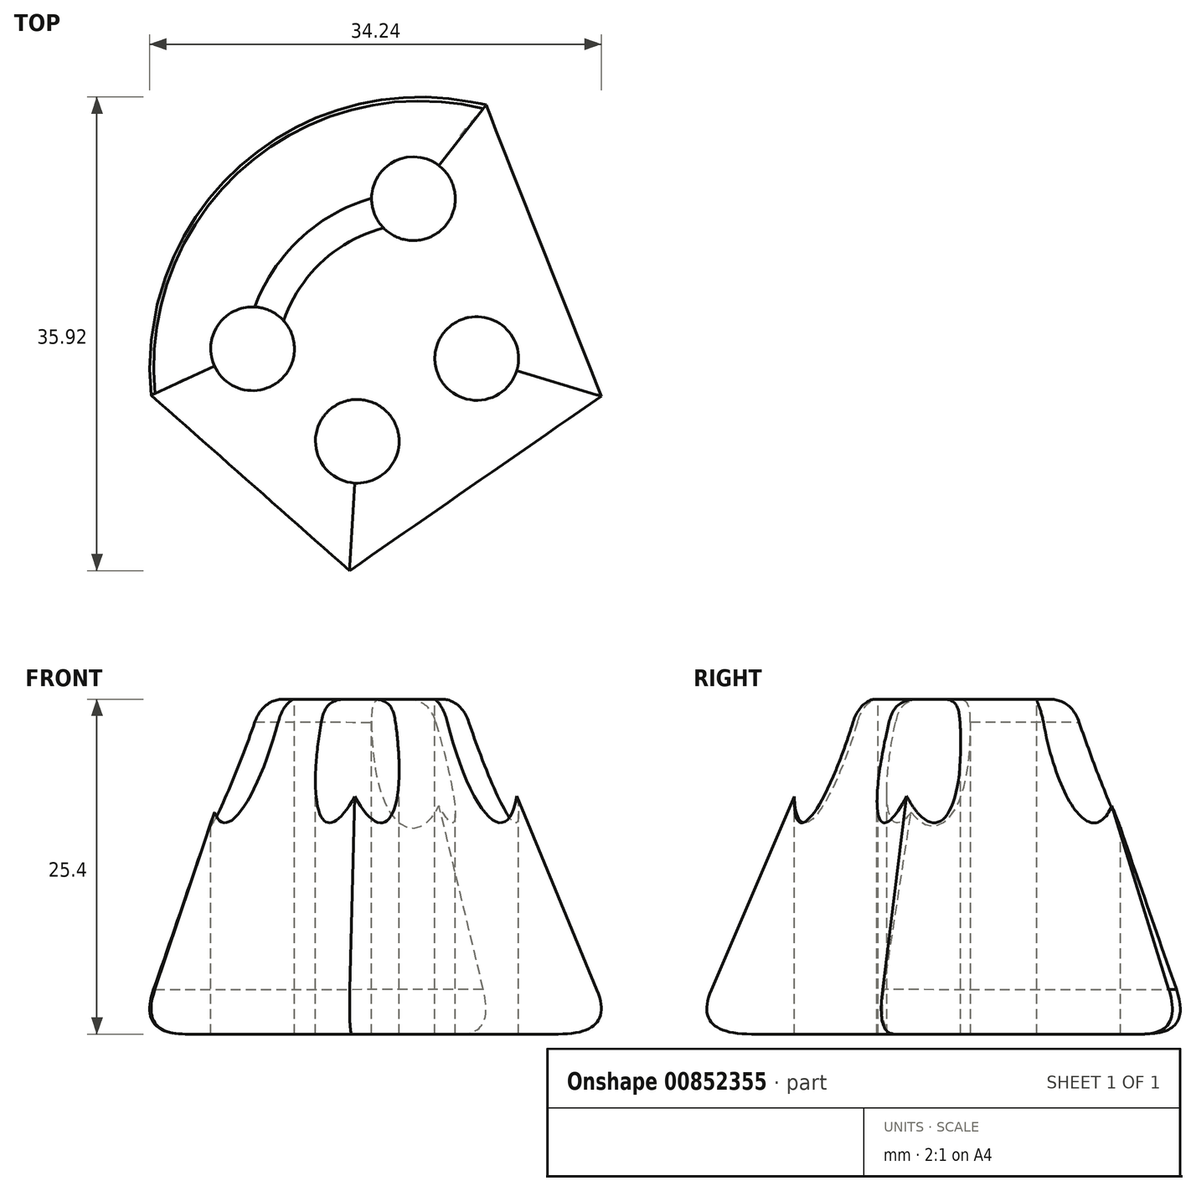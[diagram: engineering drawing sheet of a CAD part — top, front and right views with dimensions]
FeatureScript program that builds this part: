
annotation { "Feature Type Name" : "Feature", "Feature Type Description" : "" }
export const myFeature = defineFeature(function(context is Context, id is Id, definition is map)
    precondition{}
    {
        {
            var Q0;
            Q0=qCreatedBy(makeId("Top.planeOp"),FACE);
            var sketch = newSketch(context, id + "F0", { "sketchPlane" : qUnion([Q0])});
            skArc(sketch, "E0", {"start": v(-21.4, 41.04) * mm, "mid": v(-40.95, 36.53) * mm, "end": v(-48.27, 17.85) * mm});
            skLineSegment(sketch, "E1", {"start": v(-48.27, 17.85) * mm, "end": v(-32.43, 3.85) * mm});
            skLineSegment(sketch, "E2", {"start": v(-32.43, 3.85) * mm, "end": v(-12.23, 17.85) * mm});
            skLineSegment(sketch, "E3", {"start": v(-12.23, 17.85) * mm, "end": v(-21.4, 41.04) * mm});
            skSolve(sketch);
        }
        {
            var Q0;
            Q0=qCreatedBy(makeId("Top.planeOp"),FACE);
            cPlane(context, id + "F1", {"entities" : qUnion([Q0]), "cplaneType" : CPlaneType.OFFSET, "offset" : 25.4 * mm, "width" : 152.4 * mm, "height" : 152.4 * mm});
        }
        {
            var Q0;
            Q0=qCreatedBy(id+"F1.planeOp",FACE);
            var sketch = newSketch(context, id + "F2", { "sketchPlane" : qUnion([Q0])});
            skLineSegment(sketch, "E4.0", {"start": v(-31.79, 14.74) * mm, "end": v(-22.72, 21.03) * mm});
            skLineSegment(sketch, "E4.1", {"start": v(-39.72, 21.76) * mm, "end": v(-31.79, 14.74) * mm});
            skArc(sketch, "E4.2", {"start": v(-27.52, 33.15) * mm, "mid": v(-35.71, 29.7) * mm, "end": v(-39.72, 21.76) * mm});
            skLineSegment(sketch, "E4.3", {"start": v(-22.72, 21.03) * mm, "end": v(-27.52, 33.15) * mm});
            skSolve(sketch);
        }
        {
            var Q0;
            Q0=makeQuery(id+"F0.imprint","IMPRINT",FACE,{"disambiguationData":[TD([[makeQuery(id+"F0.imprint","IMPRINT",EDGE,{"derivedFrom":sQuery(id+"F0.wireOp",EDGE,"E0")}),1.0]])]});
            var Q1;
            Q1=makeQuery(id+"F2.imprint","IMPRINT",FACE,{"disambiguationData":[TD([[makeQuery(id+"F2.imprint","IMPRINT",EDGE,{"derivedFrom":sQuery(id+"F2.wireOp",EDGE,"E4.0")}),1.0]])]});
            loft(context, id + "F3", {"sheetProfilesArray" : [{ "sheetProfileEntities" : qUnion([Q0]) }, { "sheetProfileEntities" : qUnion([Q1]) }]});
        }
        {
            var Q0;
            Q0=makeQuery(id+"F3.opLoft","MID_CAP_EDGE",EDGE,{"disambiguationData":[OSD([sQuery(id+"F2.wireOp",EDGE,"E4.1"),sQuery(id+"F2.wireOp",EDGE,"E4.2"),sQuery(id+"F2.wireOp",EDGE,"E4.3")])],"capPos":1.0});
            var Q1;
            Q1=makeQuery(id+"F3.opLoft","MID_CAP_EDGE",EDGE,{"disambiguationData":[OSD([sQuery(id+"F2.wireOp",EDGE,"E4.0"),sQuery(id+"F2.wireOp",EDGE,"E4.2"),sQuery(id+"F2.wireOp",EDGE,"E4.3")])],"capPos":1.0});
            var Q2;
            Q2=makeQuery(id+"F3.opLoft","MID_CAP_EDGE",EDGE,{"disambiguationData":[OSD([sQuery(id+"F2.wireOp",EDGE,"E4.0"),sQuery(id+"F2.wireOp",EDGE,"E4.1"),sQuery(id+"F2.wireOp",EDGE,"E4.3")])],"capPos":1.0});
            var Q3;
            Q3=makeQuery(id+"F3.opLoft","MID_CAP_EDGE",EDGE,{"disambiguationData":[OSD([sQuery(id+"F2.wireOp",EDGE,"E4.0"),sQuery(id+"F2.wireOp",EDGE,"E4.1"),sQuery(id+"F2.wireOp",EDGE,"E4.2")])],"capPos":1.0});
            fillet(context, id + "F4", {"entities" : qUnion([Q0, Q1, Q2, Q3]), "radius" : 2.54 * mm, "tangentPropagation" : true, "rho" : 0.5, "crossSection" : FilletCrossSection.CONIC, "allowEdgeOverflow" : false});
        }
        {
            var Q0;
            Q0=makeQuery(id+"F3.opLoft","MID_CAP_EDGE",EDGE,{"disambiguationData":[OSD([sQuery(id+"F0.wireOp",EDGE,"E0"),sQuery(id+"F0.wireOp",EDGE,"E1"),sQuery(id+"F0.wireOp",EDGE,"E3")])],"capPos":0.0});
            var Q1;
            Q1=makeQuery(id+"F3.opLoft","MID_CAP_EDGE",EDGE,{"disambiguationData":[OSD([sQuery(id+"F0.wireOp",EDGE,"E0"),sQuery(id+"F0.wireOp",EDGE,"E2"),sQuery(id+"F0.wireOp",EDGE,"E3")])],"capPos":0.0});
            var Q2;
            Q2=makeQuery(id+"F3.opLoft","MID_CAP_EDGE",EDGE,{"disambiguationData":[OSD([sQuery(id+"F0.wireOp",EDGE,"E1"),sQuery(id+"F0.wireOp",EDGE,"E2"),sQuery(id+"F0.wireOp",EDGE,"E3")])],"capPos":0.0});
            var Q3;
            Q3=makeQuery(id+"F3.opLoft","MID_CAP_EDGE",EDGE,{"disambiguationData":[OSD([sQuery(id+"F0.wireOp",EDGE,"E0"),sQuery(id+"F0.wireOp",EDGE,"E1"),sQuery(id+"F0.wireOp",EDGE,"E2")])],"capPos":0.0});
            fillet(context, id + "F5", {"entities" : qUnion([Q0, Q1, Q2, Q3]), "radius" : 2.54 * mm, "tangentPropagation" : true, "rho" : 0.5, "crossSection" : FilletCrossSection.CONIC, "allowEdgeOverflow" : false});
        }
        {
            var Q0;
            Q0=sQuery(id+"F2.wireOp",VERTEX,"E4.1.start");
            var Q1;
            Q1=sQuery(id+"F2.wireOp",VERTEX,"E4.0.start");
            var Q2;
            Q2=sQuery(id+"F2.wireOp",VERTEX,"E4.0.end");
            var Q3;
            Q3=sQuery(id+"F2.wireOp",VERTEX,"E4.2.start");
            var Q4;
            Q4=makeQuery(id+"F3.opLoft","SWEPT_BODY",BODY,{"disambiguationData":[OSD([makeQuery(id+"F0.imprint","IMPRINT",FACE,{"disambiguationData":[TD([[makeQuery(id+"F0.imprint","IMPRINT",EDGE,{"derivedFrom":sQuery(id+"F0.wireOp",EDGE,"E0")}),1.0]])]}),makeQuery(id+"F2.imprint","IMPRINT",FACE,{"disambiguationData":[TD([[makeQuery(id+"F2.imprint","IMPRINT",EDGE,{"derivedFrom":sQuery(id+"F2.wireOp",EDGE,"E4.0")}),1.0]])]})])]});
            hole(context, id + "F6", {"style" : HoleStyle.SIMPLE, "endStyle" : HoleEndStyle.THROUGH, "holeDiameter" : 6.35 * mm, "majorDiameter" : 6.35 * mm, "isTappedThrough" : true, "tappedDepth" : 12.7 * mm, "tapClearance" : 3, "locations" : qUnion([Q0, Q1, Q2, Q3]), "scope" : qUnion([Q4])});
        }
    });
